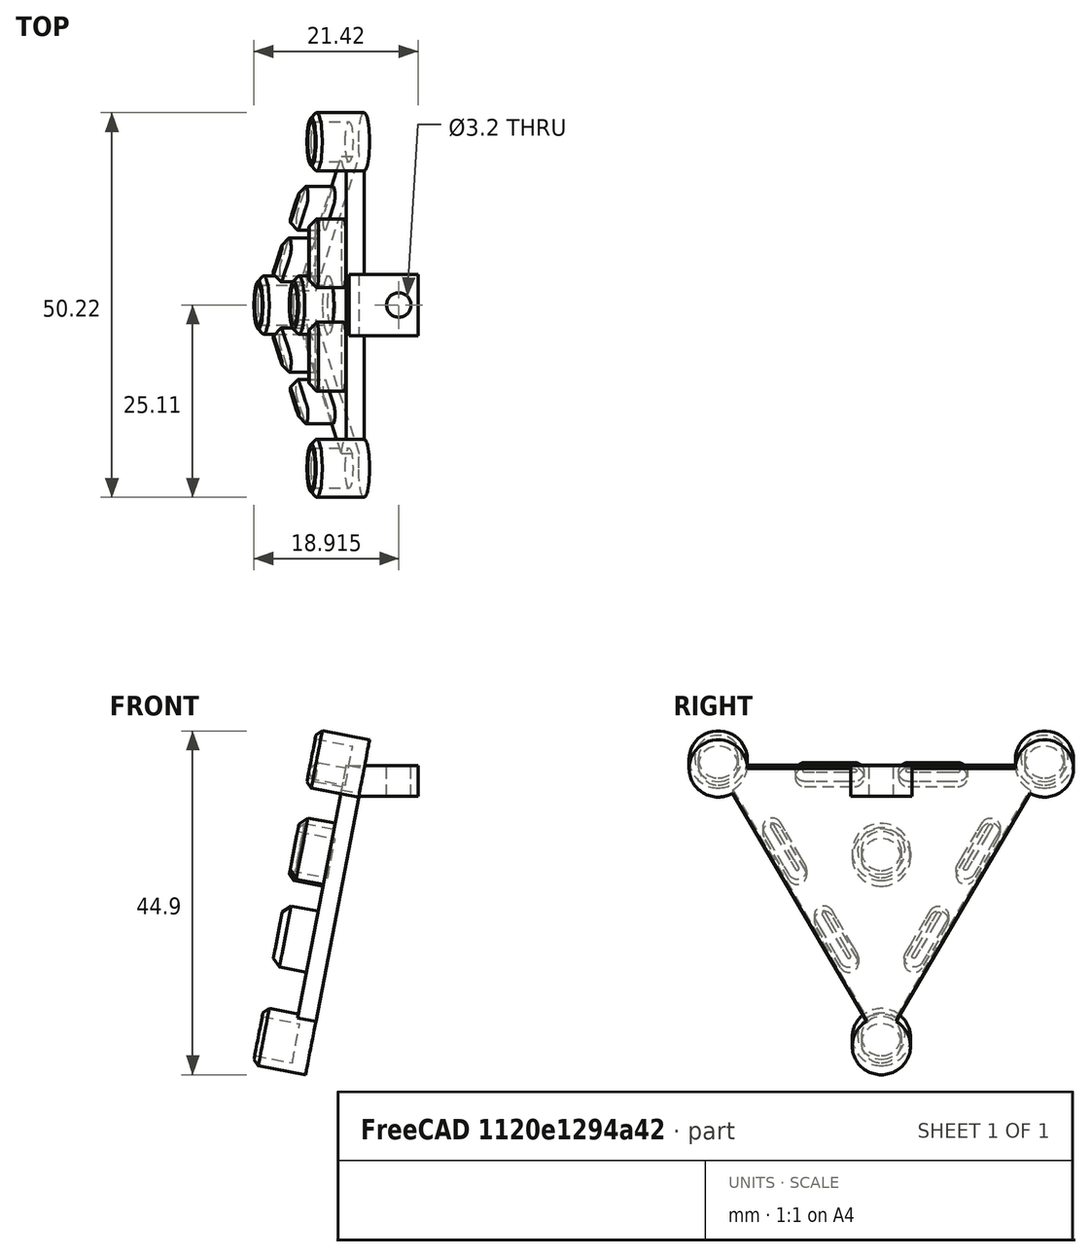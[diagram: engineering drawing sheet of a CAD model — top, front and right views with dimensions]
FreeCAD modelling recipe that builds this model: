
FCSTD DOCUMENT  (FreeCAD 0.20R27422 (Git))
Label: Inner_rev3
License: All rights reserved
LicenseURL: http://en.wikipedia.org/wiki/All_rights_reserved
objects: PartDesign::Line×5, Part::Chamfer×2, Part::Part2DObjectPython×1, Part::Feature×1, PartDesign::CoordinateSystem×1, App::Part×1
note: 10 computed .brp shape members not serialized (recipe doc carries the construction recipe); baked Part::Feature solids carry a one-line shape summary decoded from their .brp

FEATURE [Part::Part2DObjectPython] Line  # Draft 2D object (typed FeaturePython)
  Area = 0
  ChamferSize = 0
  Closed = false
  End = (-60.4609,0,-2.48e-14)
  FilletRadius = 0
  Length = 60.4609
  MakeFace = true
  Points = (2) [(0,0,0),(-60.4609,0,-2.4803e-14)]
  Start = (0,0,0)
  Subdivisions = 0
FEATURE [Part::Feature] Shape002  label="inner_center_rev3"
  shape: bbox 21.55 x 50.22 x 45.04 mm, 88 faces (baked)
FEATURE [PartDesign::CoordinateSystem] LCS_0
  AttacherType = Attacher::AttachEngine3D
  MapMode = 2
  Support = -> [X_Axis]
FEATURE [Part::Chamfer] Chamfer
  Base = -> Shape002
  Edges = 6 edges r=1: [Edge88,Edge89,Edge100,Edge112,Edge115,Edge128]
FEATURE [Part::Chamfer] Chamfer001
  Base = -> Chamfer
  Edges = 4 edges r=0.7: [Edge57,Edge71,Edge76,Edge118]
FEATURE [PartDesign::Line] HoleAxis_1  label="bottom_axis"
  AttacherType = Attacher::AttachEngineLine
  Length = 7.32715
  MapMode = 19
  Placement = pos=(-58.1106,-1.2e-14,-13.956) rot=(0,1,0;1.75951rad)
  ResizeMode = 1
  Support = -> [Chamfer001]
FEATURE [PartDesign::Line] HoleAxis_2  label="left_top_axis"
  AttacherType = Attacher::AttachEngineLine
  Length = 7.32715
  MapMode = 19
  Placement = pos=(-51.1858,21.3123,22.3027) rot=(0,1,0;1.75951rad)
  ResizeMode = 1
  Support = -> [Chamfer001]
FEATURE [PartDesign::Line] HoleAxis_3  label="center_axis"
  AttacherType = Attacher::AttachEngineLine
  Length = 7.32715
  MapMode = 19
  Placement = pos=(-53.4941,-5e-15,10.2165) rot=(0,1,0;1.75951rad)
  ResizeMode = 1
  Support = -> [Chamfer001]
FEATURE [PartDesign::Line] HoleAxis_4  label="right_top_axis"
  AttacherType = Attacher::AttachEngineLine
  Length = 7.32715
  MapMode = 19
  Placement = pos=(-51.1858,-21.3123,22.3027) rot=(0,1,0;1.75951rad)
  ResizeMode = 1
  Support = -> [Chamfer001]
FEATURE [PartDesign::Line] HoleAxis_5  label="screw_axis"
  AttacherType = Attacher::AttachEngineLine
  Length = 4.50902
  MapMode = 19
  Placement = pos=(-39.7746,0,21.3647) rot=(0,0,1;0rad)
  ResizeMode = 1
  Support = -> [Chamfer001]
FEATURE [App::Part] inner_center_part_rev3
  Group = -> [LCS_0,Shape002,Chamfer,Chamfer001,HoleAxis_1,HoleAxis_2,HoleAxis_3,HoleAxis_4,HoleAxis_5]
  Origin = -> Origin
